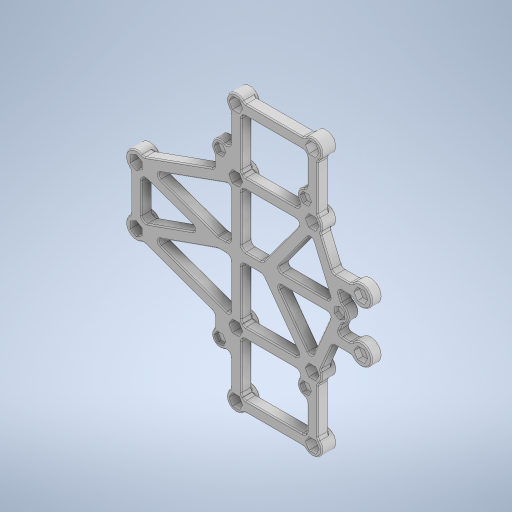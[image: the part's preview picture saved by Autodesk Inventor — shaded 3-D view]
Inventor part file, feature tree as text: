
AUTODESK INVENTOR PART (.ipt)
format: ipt  version: 2024.2 (Build 282272000, 272)  size: 1,457,664 bytes
history: native  units: mm
features: sketch x11, extrude x9, reference x8, fillet x3, other x3, hole x2
ambient origin geometry x8: Origin, YZ Plane, XZ Plane, XY Plane, X Axis, Y Axis, Z Axis, Center Point
bodies: Solid1 (feature_tree)
feature tree (36):
  extrude  "Extrusion1"  Depth=8.0mm
  extrude  "Extrusion2"  Depth=72.4mm
  extrude  "Extrusion5"  Depth=42.0mm
  extrude  "Extrusion3"  Depth=10.0mm
  extrude  "Extrusion4"  Depth=16.0mm
  extrude  "Extrusion6"  Depth=5.0mm
  hole  "Hole1"  [1 undecoded]
  hole  "Hole2"  [1 undecoded]
  fillet  "Fillet1"  Radius=5.0mm
  fillet  "Fillet2"  Radius=2.5mm
  fillet  "Fillet4"  Radius=2.5mm
  extrude  "Extrusion7"  Depth=5.0mm
  extrude  "Extrusion8"  Depth=5.0mm
  extrude  "Extrusion9"  Depth=2.0mm
  sketch  "Sketch2"  dims[d1=65.0mm d2=8.0mm]
  reference  "Reference10"
  reference  "Reference11"
  reference  "Reference12"
  reference  "Reference13"
  reference  "Reference14"
  reference  "Reference15"
  reference  "Reference16"
  reference  "Reference17"
  sketch  "Sketch3"  dims[d3=4.8mm d4=72.4mm]
  sketch  "Sketch4"  dims[d5=96.0mm d8=42.0mm]
  sketch  "Sketch5"  dims[d9=10.0mm d10=27.0mm]
  sketch  "Sketch6"  dims[d11=5.0mm d13=16.0mm]
  sketch  "Sketch7"  dims[d14=65.0mm d15=5.0mm]
  sketch  "Sketch8"  dims[d16=5.0mm d17=5.0mm]
  sketch  "Sketch9"  dims[d18=2.5mm d19=2.5mm d21=5.0mm d22=2.5mm d23=2.5mm]
  sketch  "Sketch10"  dims[d24=2.5mm d27=5.0mm]
  sketch  "Sketch11"  dims[d28=5.0mm d29=5.0mm]
  sketch  "Sketch12"  dims[d30=5.0mm d31=5.0mm d32=2.5mm d33=2.5mm d34=5.0mm d35=2.5mm d36=10.0mm d37=5.0mm d38=5.0mm d39=2.5mm d40=2.5mm d41=6.0mm d42=5.0mm d43=0.0mm d44=5.6mm d45=5.6mm d46=2.5mm d47=2.5mm d48=10.0mm d49=5.0mm d50=2.5mm d51=10.0mm d52=12.0mm d53=5.6mm d54=4.5mm d55=0.0mm d56=1.9mm d57=0.0mm d58=4.5mm d59=0.0mm d60=3.5mm d61=6.0mm d62=4.0mm d63=2.0mm d64=90.0deg d65=1.0mm d66=0.0mm d67=2.0mm d68=1.5mm d70=5.25mm d71=6.0mm d72=4.0mm d73=2.0mm d74=90.0deg d75=1.6mm d76=0.0mm d77=2.5mm d78=0.0mm d79=2.0mm d80=0.0mm d81=0.5mm d82=0.2mm d83=0.0mm d84=0.2mm d85=0.0mm d86=0.2mm d87=0.0mm]
  other  "<userpath>\Desktop\scioly-robot-tour\Hardware\ipt\v4\v4assembly.iam"
  other  "v4assembly.iam"
  other  "v4motormount:1"
note: 2 required parameter values undecoded (feature->parameter linkage not recoverable at this tier; creation-order binding heuristic only, values carry confidence <= 0.55)
